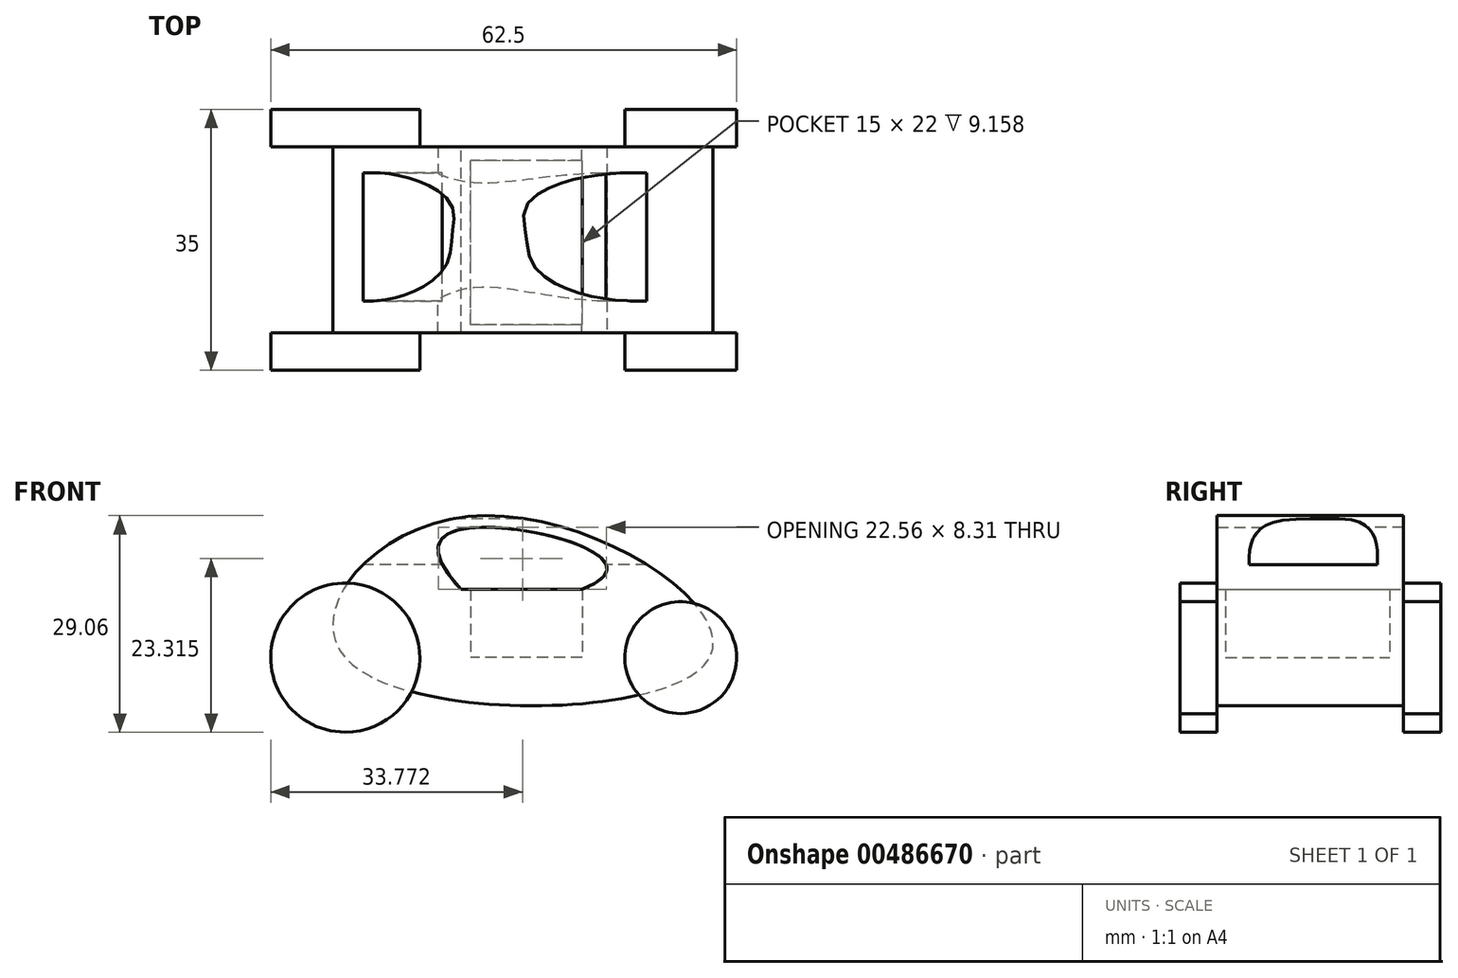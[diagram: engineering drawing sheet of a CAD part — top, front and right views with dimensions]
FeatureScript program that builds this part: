
annotation { "Feature Type Name" : "Feature", "Feature Type Description" : "" }
export const myFeature = defineFeature(function(context is Context, id is Id, definition is map)
    precondition{}
    {
        {
            var Q0;
            Q0=qCreatedBy(makeId("Front.planeOp"),FACE);
            var sketch = newSketch(context, id + "F0", { "sketchPlane" : qUnion([Q0])});
            skFitSpline(sketch, "E0", {"points": [v(0, 0) * mm, v(48.87, 0) * mm, v(16.36, 18.92) * mm, v(0, 0) * mm]});
            skSolve(sketch);
        }
        {
            var Q0;
            Q0 = qSketchRegion(id + "F0", true);
            extrude(context, id + "F1", {"entities" : qUnion([Q0]), "depth" : 25 * mm});
        }
        {
            var Q0;
            Q0=makeQuery(id+"F1.opExtrude","CAP_FACE",FACE,{"disambiguationData":[OSD([sQuery(id+"F0.wireOp",EDGE,"E0")])],"isStart":true});
            var sketch = newSketch(context, id + "F2", { "sketchPlane" : qUnion([Q0])});
            skCircle(sketch, "E1", {"center": v(0, 0) * mm, "radius": 10 * mm});
            skCircle(sketch, "E2", {"center": v(-45, 0) * mm, "radius": 7.5 * mm});
            skSolve(sketch);
        }
        {
            var Q0;
            Q0 = qSketchRegion(id + "F2", true);
            extrude(context, id + "F3", {"entities" : qUnion([Q0]), "operationType" : NewBodyOperationType.ADD, "depth" : 5 * mm});
        }
        {
            var Q0;
            Q0=makeQuery(id+"F1.opExtrude","CAP_FACE",FACE,{"disambiguationData":[OSD([sQuery(id+"F0.wireOp",EDGE,"E0")])],"isStart":false});
            var sketch = newSketch(context, id + "F4", { "sketchPlane" : qUnion([Q0])});
            skCircle(sketch, "E3", {"center": v(0, 0) * mm, "radius": 10 * mm});
            skCircle(sketch, "E4", {"center": v(45, 0) * mm, "radius": 7.5 * mm});
            skSolve(sketch);
        }
        {
            var Q0;
            Q0 = qSketchRegion(id + "F4", true);
            extrude(context, id + "F5", {"entities" : qUnion([Q0]), "operationType" : NewBodyOperationType.ADD, "depth" : 5 * mm});
        }
        {
            var Q0;
            Q0=makeQuery(id+"F1.opExtrude","CAP_FACE",FACE,{"disambiguationData":[OSD([sQuery(id+"F0.wireOp",EDGE,"E0")])],"isStart":true});
            var sketch = newSketch(context, id + "F6", { "sketchPlane" : qUnion([Q0])});
            skLineSegment(sketch, "E5", {"start": v(-31.74, 9.16) * mm, "end": v(-15.53, 9.16) * mm});
            skFitSpline(sketch, "E6", {"points": [v(-15.53, 9.16) * mm, v(-22.3, 17.26) * mm, v(-31.74, 9.16) * mm], "startDerivative": vector(44.44, 47.07) * mm, "endDerivative": vector(49.82, -19.41) * mm});
            skSolve(sketch);
        }
        {
            var Q0;
            Q0 = qSketchRegion(id + "F6", true);
            extrude(context, id + "F7", {"entities" : qUnion([Q0]), "operationType" : NewBodyOperationType.REMOVE, "oppositeDirection" : true, "depth" : 25 * mm});
        }
        {
            var Q0;
            Q0=qCreatedBy(makeId("Right.planeOp"),FACE);
            var sketch = newSketch(context, id + "F8", { "sketchPlane" : qUnion([Q0])});
            skLineSegment(sketch, "E7", {"start": v(-20.7, 12.48) * mm, "end": v(-3.53, 12.48) * mm});
            skFitSpline(sketch, "E8", {"points": [v(-3.53, 12.48) * mm, v(-11.83, 18.62) * mm, v(-20.7, 12.48) * mm], "startDerivative": vector(3.14, 41.07) * mm, "endDerivative": vector(2.1, -37.92) * mm});
            skSolve(sketch);
        }
        {
            var Q0;
            Q0 = qSketchRegion(id + "F8", true);
            extrude(context, id + "F9", {"entities" : qUnion([Q0]), "operationType" : NewBodyOperationType.REMOVE, "depth" : 50 * mm});
        }
        {
            var Q0;
            Q0=qCreatedBy(makeId("Top.planeOp"),FACE);
            var sketch = newSketch(context, id + "F10", { "sketchPlane" : qUnion([Q0])});
            skLineSegment(sketch, "E9.bottom", {"start": v(31.8, -23.88) * mm, "end": v(16.8, -23.88) * mm});
            skLineSegment(sketch, "E9.top", {"start": v(31.8, -1.88) * mm, "end": v(16.8, -1.88) * mm});
            skLineSegment(sketch, "E9.left", {"start": v(31.8, -23.88) * mm, "end": v(31.8, -1.88) * mm});
            skLineSegment(sketch, "E9.right", {"start": v(16.8, -23.88) * mm, "end": v(16.8, -1.88) * mm});
            skPoint(sketch, "E9.middle", {"position": v(24.3, -12.88) * mm});
            skSolve(sketch);
        }
        {
            var Q0;
            Q0 = qSketchRegion(id + "F10", true);
            extrude(context, id + "F11", {"entities" : qUnion([Q0]), "operationType" : NewBodyOperationType.REMOVE, "depth" : 11.7 * mm});
        }
    });
